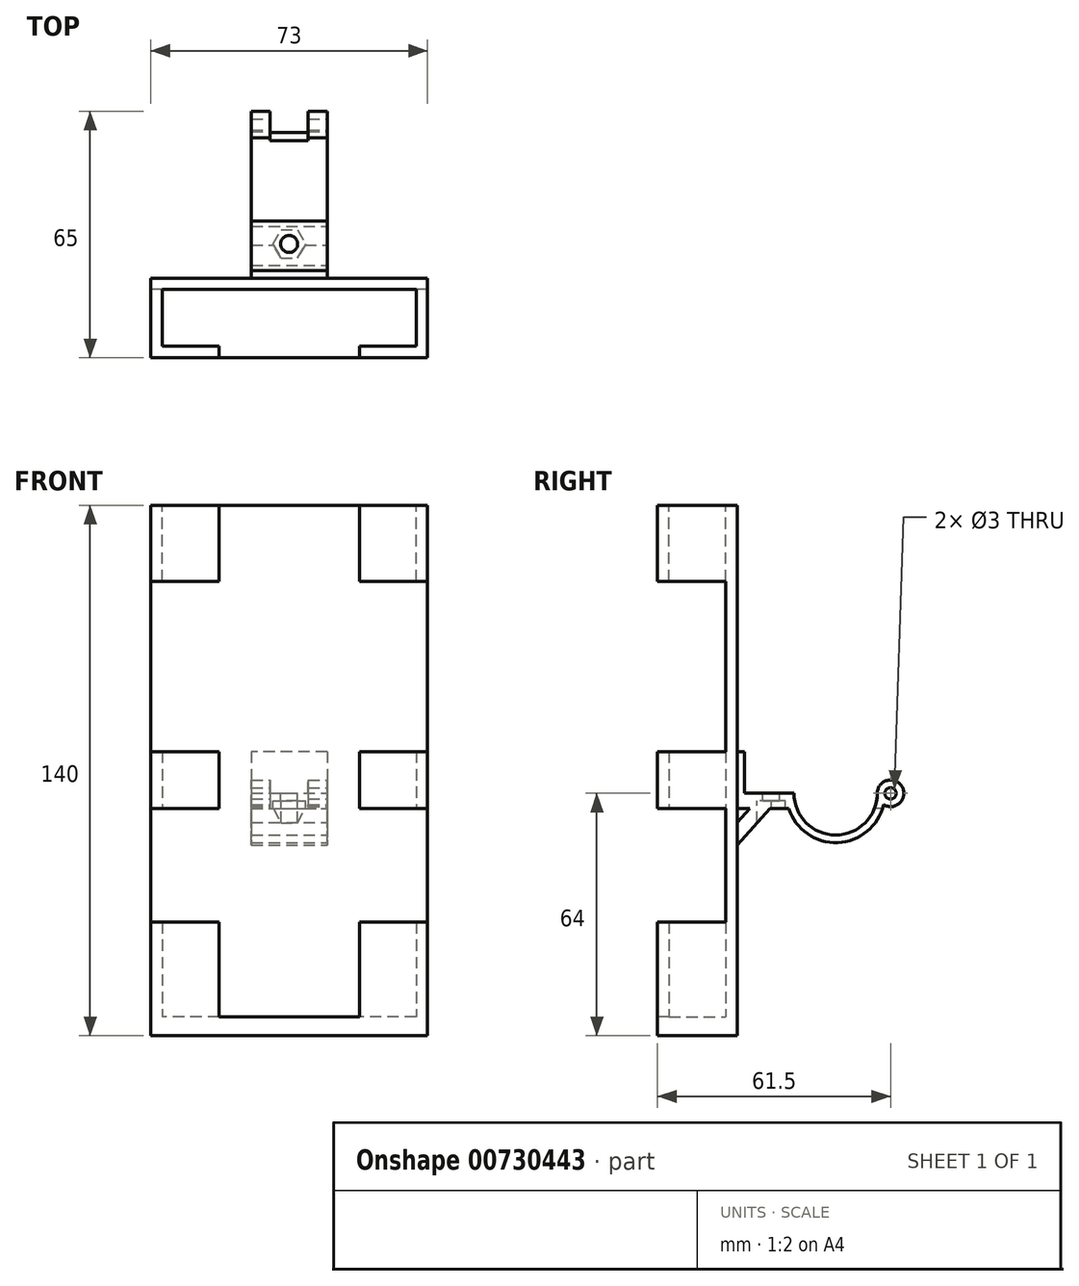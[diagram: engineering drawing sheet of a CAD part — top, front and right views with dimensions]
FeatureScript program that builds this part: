
annotation { "Feature Type Name" : "Feature", "Feature Type Description" : "" }
export const myFeature = defineFeature(function(context is Context, id is Id, definition is map)
    precondition{}
    {
        {
            var Q0;
            Q0=qCreatedBy(makeId("Top.planeOp"),FACE);
            var sketch = newSketch(context, id + "F0", { "sketchPlane" : qUnion([Q0])});
            skLineSegment(sketch, "E0", {"start": v(-18.5, -21) * mm, "end": v(-36.5, -21) * mm});
            skLineSegment(sketch, "E1", {"start": v(-36.5, -21) * mm, "end": v(-36.5, 0) * mm});
            skLineSegment(sketch, "E2", {"start": v(-36.5, 0) * mm, "end": v(36.5, 0) * mm});
            skLineSegment(sketch, "E3", {"start": v(36.5, 0) * mm, "end": v(36.5, -21) * mm});
            skLineSegment(sketch, "E4", {"start": v(36.5, -21) * mm, "end": v(18.5, -21) * mm});
            skLineSegment(sketch, "E5", {"start": v(18.5, -18) * mm, "end": v(33.5, -18) * mm});
            skLineSegment(sketch, "E6", {"start": v(33.5, -18) * mm, "end": v(33.5, -3) * mm});
            skLineSegment(sketch, "E7", {"start": v(33.5, -3) * mm, "end": v(-33.5, -3) * mm});
            skLineSegment(sketch, "E8", {"start": v(-33.5, -3) * mm, "end": v(-33.5, -18) * mm});
            skLineSegment(sketch, "E9", {"start": v(-33.5, -18) * mm, "end": v(-18.5, -18) * mm});
            skLineSegment(sketch, "E10", {"start": v(-18.5, -18) * mm, "end": v(-18.5, -21) * mm});
            skLineSegment(sketch, "E11", {"start": v(18.5, -18) * mm, "end": v(18.5, -21) * mm});
            skSolve(sketch);
        }
        {
            var Q0;
            Q0=makeQuery(id+"F0.imprint","IMPRINT",FACE,{"disambiguationData":[TD([[makeQuery(id+"F0.imprint","IMPRINT",EDGE,{"derivedFrom":sQuery(id+"F0.wireOp",EDGE,"E0")}),-1.0]])]});
            extrude(context, id + "F1", {"entities" : qUnion([Q0]), "depth" : 30 * mm, "offsetDistance" : 25 * mm});
        }
        {
            var Q0;
            Q0=qCreatedBy(makeId("Top.planeOp"),FACE);
            var sketch = newSketch(context, id + "F2", { "sketchPlane" : qUnion([Q0])});
            skLineSegment(sketch, "E12.bottom", {"start": v(36.5, 0) * mm, "end": v(-36.5, 0) * mm});
            skLineSegment(sketch, "E12.top", {"start": v(36.5, -21) * mm, "end": v(-36.5, -21) * mm});
            skLineSegment(sketch, "E12.left", {"start": v(36.5, 0) * mm, "end": v(36.5, -21) * mm});
            skLineSegment(sketch, "E12.right", {"start": v(-36.5, 0) * mm, "end": v(-36.5, -21) * mm});
            skLineSegment(sketch, "E13.bottom", {"start": v(36.5, 0) * mm, "end": v(36.5, 0) * mm});
            skLineSegment(sketch, "E13.top", {"start": v(36.5, -21) * mm, "end": v(36.5, -21) * mm});
            skSolve(sketch);
        }
        {
            var Q0;
            Q0 = qSketchRegion(id + "F2", true);
            extrude(context, id + "F3", {"entities" : qUnion([Q0]), "operationType" : NewBodyOperationType.ADD, "depth" : 5 * mm, "offsetDistance" : 25 * mm});
        }
        {
            var Q0;
            Q0=qCreatedBy(makeId("Front.planeOp"),FACE);
            var sketch = newSketch(context, id + "F4", { "sketchPlane" : qUnion([Q0])});
            skLineSegment(sketch, "E14.bottom", {"start": v(-36.5, 140) * mm, "end": v(36.5, 140) * mm});
            skLineSegment(sketch, "E14.top", {"start": v(-36.5, 30) * mm, "end": v(36.5, 30) * mm});
            skLineSegment(sketch, "E14.left", {"start": v(-36.5, 140) * mm, "end": v(-36.5, 30) * mm});
            skLineSegment(sketch, "E14.right", {"start": v(36.5, 140) * mm, "end": v(36.5, 30) * mm});
            skSolve(sketch);
        }
        {
            var Q0;
            Q0 = qSketchRegion(id + "F4", true);
            extrude(context, id + "F5", {"entities" : qUnion([Q0]), "operationType" : NewBodyOperationType.ADD, "depth" : 3 * mm, "offsetDistance" : 25 * mm});
        }
        {
            var Q0;
            Q0=qCreatedBy(makeId("Front.planeOp"),FACE);
            cPlane(context, id + "F6", {"entities" : qUnion([Q0]), "cplaneType" : CPlaneType.OFFSET, "offset" : 34 * mm, "oppositeDirection" : true, "width" : 150 * mm, "height" : 150 * mm});
        }
        {
            var Q0;
            Q0=makeQuery(id+"F2.imprint","IMPRINT",FACE,{"disambiguationData":[TD([[makeQuery(id+"F2.imprint","IMPRINT",EDGE,{"derivedFrom":sQuery(id+"F2.wireOp",EDGE,"E12.bottom")}),1.0]])]});
            cPlane(context, id + "F7", {"entities" : qUnion([Q0]), "cplaneType" : CPlaneType.OFFSET, "offset" : 60 * mm, "width" : 150 * mm, "height" : 150 * mm});
        }
        {
            var Q0;
            Q0=qCreatedBy(id+"F7.planeOp",FACE);
            var sketch = newSketch(context, id + "F8", { "sketchPlane" : qUnion([Q0])});
            skLineSegment(sketch, "E15.0", {"start": v(-33.5, -18) * mm, "end": v(-18.5, -18) * mm});
            skLineSegment(sketch, "E16.0", {"start": v(-33.5, -3) * mm, "end": v(-33.5, -18) * mm});
            skLineSegment(sketch, "E17.0", {"start": v(-18.5, -18) * mm, "end": v(-18.5, -21) * mm});
            skLineSegment(sketch, "E18.0", {"start": v(18.5, -18) * mm, "end": v(33.5, -18) * mm});
            skLineSegment(sketch, "E19.0", {"start": v(18.5, -18) * mm, "end": v(18.5, -21) * mm});
            skLineSegment(sketch, "E20.0", {"start": v(36.5, -21) * mm, "end": v(18.5, -21) * mm});
            skLineSegment(sketch, "E21.0", {"start": v(-18.5, -21) * mm, "end": v(-36.5, -21) * mm});
            skLineSegment(sketch, "E22.0", {"start": v(36.5, -3) * mm, "end": v(36.5, -21) * mm});
            skLineSegment(sketch, "E23.0", {"start": v(33.5, -18) * mm, "end": v(33.5, -3) * mm});
            skLineSegment(sketch, "E24.0", {"start": v(33.5, -3) * mm, "end": v(36.5, -3) * mm});
            skLineSegment(sketch, "E25", {"start": v(-36.5, -21) * mm, "end": v(-36.5, -3) * mm});
            skLineSegment(sketch, "E26", {"start": v(-36.5, -3) * mm, "end": v(-33.5, -3) * mm});
            skSolve(sketch);
        }
        {
            var Q0;
            Q0 = qSketchRegion(id + "F8", true);
            extrude(context, id + "F9", {"entities" : qUnion([Q0]), "operationType" : NewBodyOperationType.ADD, "depth" : 15 * mm, "offsetDistance" : 25 * mm});
        }
        {
            var Q0;
            Q0=qCreatedBy(id+"F7.planeOp",FACE);
            cPlane(context, id + "F10", {"entities" : qUnion([Q0]), "cplaneType" : CPlaneType.OFFSET, "offset" : 80 * mm, "width" : 150 * mm, "height" : 150 * mm});
        }
        {
            var Q0;
            Q0=qCreatedBy(id+"F10.planeOp",FACE);
            var sketch = newSketch(context, id + "F11", { "sketchPlane" : qUnion([Q0])});
            skLineSegment(sketch, "E27.0.0", {"start": v(-33.5, -3) * mm, "end": v(-36.5, -3) * mm});
            skLineSegment(sketch, "E27.0.1", {"start": v(-36.5, -3) * mm, "end": v(-36.5, -21) * mm});
            skLineSegment(sketch, "E27.0.2", {"start": v(-36.5, -21) * mm, "end": v(-18.5, -21) * mm});
            skLineSegment(sketch, "E27.0.3", {"start": v(-18.5, -21) * mm, "end": v(-18.5, -18) * mm});
            skLineSegment(sketch, "E27.0.4", {"start": v(-18.5, -18) * mm, "end": v(-33.5, -18) * mm});
            skLineSegment(sketch, "E27.0.5", {"start": v(-33.5, -18) * mm, "end": v(-33.5, -3) * mm});
            skLineSegment(sketch, "E28.0.0", {"start": v(36.5, -3) * mm, "end": v(33.5, -3) * mm});
            skLineSegment(sketch, "E28.0.1", {"start": v(33.5, -3) * mm, "end": v(33.5, -18) * mm});
            skLineSegment(sketch, "E28.0.2", {"start": v(33.5, -18) * mm, "end": v(18.5, -18) * mm});
            skLineSegment(sketch, "E28.0.3", {"start": v(18.5, -18) * mm, "end": v(18.5, -21) * mm});
            skLineSegment(sketch, "E28.0.4", {"start": v(18.5, -21) * mm, "end": v(36.5, -21) * mm});
            skLineSegment(sketch, "E28.0.5", {"start": v(36.5, -21) * mm, "end": v(36.5, -3) * mm});
            skSolve(sketch);
        }
        {
            var Q0;
            Q0 = qSketchRegion(id + "F11", true);
            extrude(context, id + "F12", {"entities" : qUnion([Q0]), "operationType" : NewBodyOperationType.ADD, "oppositeDirection" : true, "depth" : 20 * mm, "offsetDistance" : 25 * mm});
        }
        {
            var Q0;
            Q0=qCreatedBy(id+"F7.planeOp",FACE);
            var sketch = newSketch(context, id + "F13", { "sketchPlane" : qUnion([Q0])});
            skLineSegment(sketch, "E29.bottom", {"start": v(10, 0) * mm, "end": v(-10, 0) * mm});
            skLineSegment(sketch, "E29.top", {"start": v(10, 15) * mm, "end": v(-10, 15) * mm});
            skLineSegment(sketch, "E29.left", {"start": v(10, 0) * mm, "end": v(10, 15) * mm});
            skLineSegment(sketch, "E29.right", {"start": v(-10, 0) * mm, "end": v(-10, 15) * mm});
            skSolve(sketch);
        }
        {
            var Q0;
            Q0 = qSketchRegion(id + "F13", true);
            extrude(context, id + "F14", {"entities" : qUnion([Q0]), "operationType" : NewBodyOperationType.ADD, "depth" : 15 * mm, "offsetDistance" : 25 * mm});
        }
        {
            var Q0;
            Q0=makeQuery(id+"F14.opExtrude","SWEPT_FACE",FACE,{"disambiguationData":[OSD([sQuery(id+"F13.wireOp",EDGE,"E29.left")])]});
            var sketch = newSketch(context, id + "F15", { "sketchPlane" : qUnion([Q0])});
            skArc(sketch, "E30", {"start": v(15, 64) * mm, "mid": v(26, 53) * mm, "end": v(37, 64) * mm});
            skArc(sketch, "E31", {"start": v(13, 64) * mm, "mid": v(24.5, 51.09) * mm, "end": v(38.66, 61.03) * mm});
            skPoint(sketch, "E31.endSnap0", {"position": v(7.5, 60) * mm});
            skLineSegment(sketch, "E32", {"start": v(13, 64) * mm, "end": v(15, 64) * mm});
            skArc(sketch, "E33", {"start": v(38.66, 61.03) * mm, "mid": v(43.56, 65.7) * mm, "end": v(37, 64) * mm});
            skSolve(sketch);
        }
        {
            var Q0;
            Q0 = qSketchRegion(id + "F15", true);
            extrude(context, id + "F16", {"entities" : qUnion([Q0]), "operationType" : NewBodyOperationType.ADD, "oppositeDirection" : true, "depth" : 20 * mm, "offsetDistance" : 25 * mm});
        }
        {
            var Q0;
            Q0=makeQuery(id+"F16.boolean.opBoolean","MERGE",FACE,{"derivedFrom":[makeQuery(id+"F14.opExtrude","SWEPT_FACE",FACE,{"disambiguationData":[OSD([sQuery(id+"F13.wireOp",EDGE,"E29.left")])]}),makeQuery(id+"F16.opExtrude","CAP_FACE",FACE,{"disambiguationData":[OSD([sQuery(id+"F15.wireOp",EDGE,"E30"),sQuery(id+"F15.wireOp",EDGE,"E31"),sQuery(id+"F15.wireOp",EDGE,"E32"),sQuery(id+"F15.wireOp",EDGE,"E33")])],"isStart":true})]});
            var sketch = newSketch(context, id + "F17", { "sketchPlane" : qUnion([Q0])});
            skCircle(sketch, "E34", {"center": v(40.5, 64) * mm, "radius": 1.5 * mm});
            skSolve(sketch);
        }
        {
            var Q0;
            Q0 = qSketchRegion(id + "F17", true);
            extrude(context, id + "F18", {"entities" : qUnion([Q0]), "operationType" : NewBodyOperationType.REMOVE, "oppositeDirection" : true, "depth" : 49.4 * mm, "offsetDistance" : 25 * mm});
        }
        {
            var Q0;
            Q0=qCreatedBy(id+"F6.planeOp",FACE);
            var sketch = newSketch(context, id + "F19", { "sketchPlane" : qUnion([Q0])});
            skLineSegment(sketch, "E35.bottom", {"start": v(5, 71) * mm, "end": v(-5, 71) * mm});
            skLineSegment(sketch, "E35.top", {"start": v(5, 60) * mm, "end": v(-5, 60) * mm});
            skLineSegment(sketch, "E35.left", {"start": v(5, 71) * mm, "end": v(5, 60) * mm});
            skLineSegment(sketch, "E35.right", {"start": v(-5, 71) * mm, "end": v(-5, 60) * mm});
            skSolve(sketch);
        }
        {
            var Q0;
            Q0 = qSketchRegion(id + "F19", true);
            extrude(context, id + "F20", {"entities" : qUnion([Q0]), "operationType" : NewBodyOperationType.REMOVE, "endBound" : BoundingType.THROUGH_ALL, "oppositeDirection" : true, "depth" : 25 * mm, "offsetDistance" : 25 * mm});
        }
        {
            var Q0;
            Q0=makeQuery(id+"F16.boolean.opBoolean","MERGE",FACE,{"derivedFrom":[makeQuery(id+"F14.opExtrude","SWEPT_FACE",FACE,{"disambiguationData":[OSD([sQuery(id+"F13.wireOp",EDGE,"E29.right")])]}),makeQuery(id+"F16.opExtrude","CAP_FACE",FACE,{"disambiguationData":[OSD([sQuery(id+"F15.wireOp",EDGE,"E30"),sQuery(id+"F15.wireOp",EDGE,"E31"),sQuery(id+"F15.wireOp",EDGE,"E32"),sQuery(id+"F15.wireOp",EDGE,"E33")])],"isStart":false})]});
            var sketch = newSketch(context, id + "F21", { "sketchPlane" : qUnion([Q0])});
            skLineSegment(sketch, "E36.bottom", {"start": v(-17, 76) * mm, "end": v(-2, 76) * mm});
            skLineSegment(sketch, "E36.top", {"start": v(-17, 64) * mm, "end": v(-2, 64) * mm});
            skLineSegment(sketch, "E36.left", {"start": v(-17, 76) * mm, "end": v(-17, 64) * mm});
            skLineSegment(sketch, "E36.right", {"start": v(-2, 76) * mm, "end": v(-2, 64) * mm});
            skCircle(sketch, "E37.0", {"center": v(-40.5, 64) * mm, "radius": 1.5 * mm, "construction": true});
            skSolve(sketch);
        }
        {
            var Q0;
            Q0 = qSketchRegion(id + "F21", true);
            extrude(context, id + "F22", {"entities" : qUnion([Q0]), "operationType" : NewBodyOperationType.REMOVE, "endBound" : BoundingType.THROUGH_ALL, "oppositeDirection" : true, "depth" : 25 * mm, "offsetDistance" : 25 * mm});
        }
        {
            var Q0;
            Q0=qCreatedBy(makeId("Right.planeOp"),FACE);
            var sketch = newSketch(context, id + "F23", { "sketchPlane" : qUnion([Q0])});
            skLineSegment(sketch, "E38", {"start": v(0, 50.34) * mm, "end": v(8.7, 60) * mm});
            skLineSegment(sketch, "E39", {"start": v(0, 56.29) * mm, "end": v(3.35, 60) * mm});
            skLineSegment(sketch, "E40", {"start": v(8.7, 60) * mm, "end": v(3.35, 60) * mm});
            skLineSegment(sketch, "E41", {"start": v(0, 56.29) * mm, "end": v(0, 50.34) * mm});
            skSolve(sketch);
        }
        {
            var Q0;
            Q0 = qSketchRegion(id + "F23", true);
            extrude(context, id + "F24", {"entities" : qUnion([Q0]), "operationType" : NewBodyOperationType.ADD, "endBound" : BoundingType.SYMMETRIC, "oppositeDirection" : true, "depth" : 20 * mm, "offsetDistance" : 25 * mm});
        }
        {
            var Q0;
            Q0=qCreatedBy(id+"F7.planeOp",FACE);
            var sketch = newSketch(context, id + "F25", { "sketchPlane" : qUnion([Q0])});
            skCircle(sketch, "E42", {"center": v(0, 9) * mm, "radius": 2.25 * mm});
            skSolve(sketch);
        }
        {
            var Q0;
            Q0 = qSketchRegion(id + "F25", true);
            extrude(context, id + "F26", {"entities" : qUnion([Q0]), "operationType" : NewBodyOperationType.REMOVE, "endBound" : BoundingType.SYMMETRIC, "oppositeDirection" : true, "depth" : 21.1 * mm, "offsetDistance" : 25 * mm});
        }
        {
            var Q0;
            Q0=makeQuery(id+"F13.imprint","IMPRINT",FACE,{"disambiguationData":[TD([[makeQuery(id+"F13.imprint","IMPRINT",EDGE,{"derivedFrom":sQuery(id+"F13.wireOp",EDGE,"E29.bottom")}),-1.0]])]});
            var sketch = newSketch(context, id + "F27", { "sketchPlane" : qUnion([Q0])});
            skArc(sketch, "E43.0", {"start": v(2.23, 8.7) * mm, "mid": v(0, 11.25) * mm, "end": v(-2.23, 8.7) * mm, "construction": true});
            skCircle(sketch, "E44.cCircle", {"center": v(0, 9) * mm, "radius": 4.33 * mm, "construction": true});
            skLineSegment(sketch, "E44.0", {"start": v(4.33, 9) * mm, "end": v(2.17, 5.25) * mm});
            skLineSegment(sketch, "E44.1", {"start": v(2.17, 5.25) * mm, "end": v(-2.17, 5.25) * mm});
            skLineSegment(sketch, "E44.2", {"start": v(-2.17, 5.25) * mm, "end": v(-4.33, 9) * mm});
            skLineSegment(sketch, "E44.3", {"start": v(-4.33, 9) * mm, "end": v(-2.17, 12.75) * mm});
            skLineSegment(sketch, "E44.4", {"start": v(-2.17, 12.75) * mm, "end": v(2.17, 12.75) * mm});
            skLineSegment(sketch, "E44.5", {"start": v(2.17, 12.75) * mm, "end": v(4.33, 9) * mm});
            skSolve(sketch);
        }
        {
            var Q0;
            Q0 = qSketchRegion(id + "F27", true);
            extrude(context, id + "F28", {"entities" : qUnion([Q0]), "operationType" : NewBodyOperationType.REMOVE, "oppositeDirection" : true, "depth" : 10 * mm, "offsetDistance" : 25 * mm, "hasSecondDirection" : true, "secondDirectionOppositeDirection" : false, "secondDirectionDepth" : 2 * mm});
        }
    });
